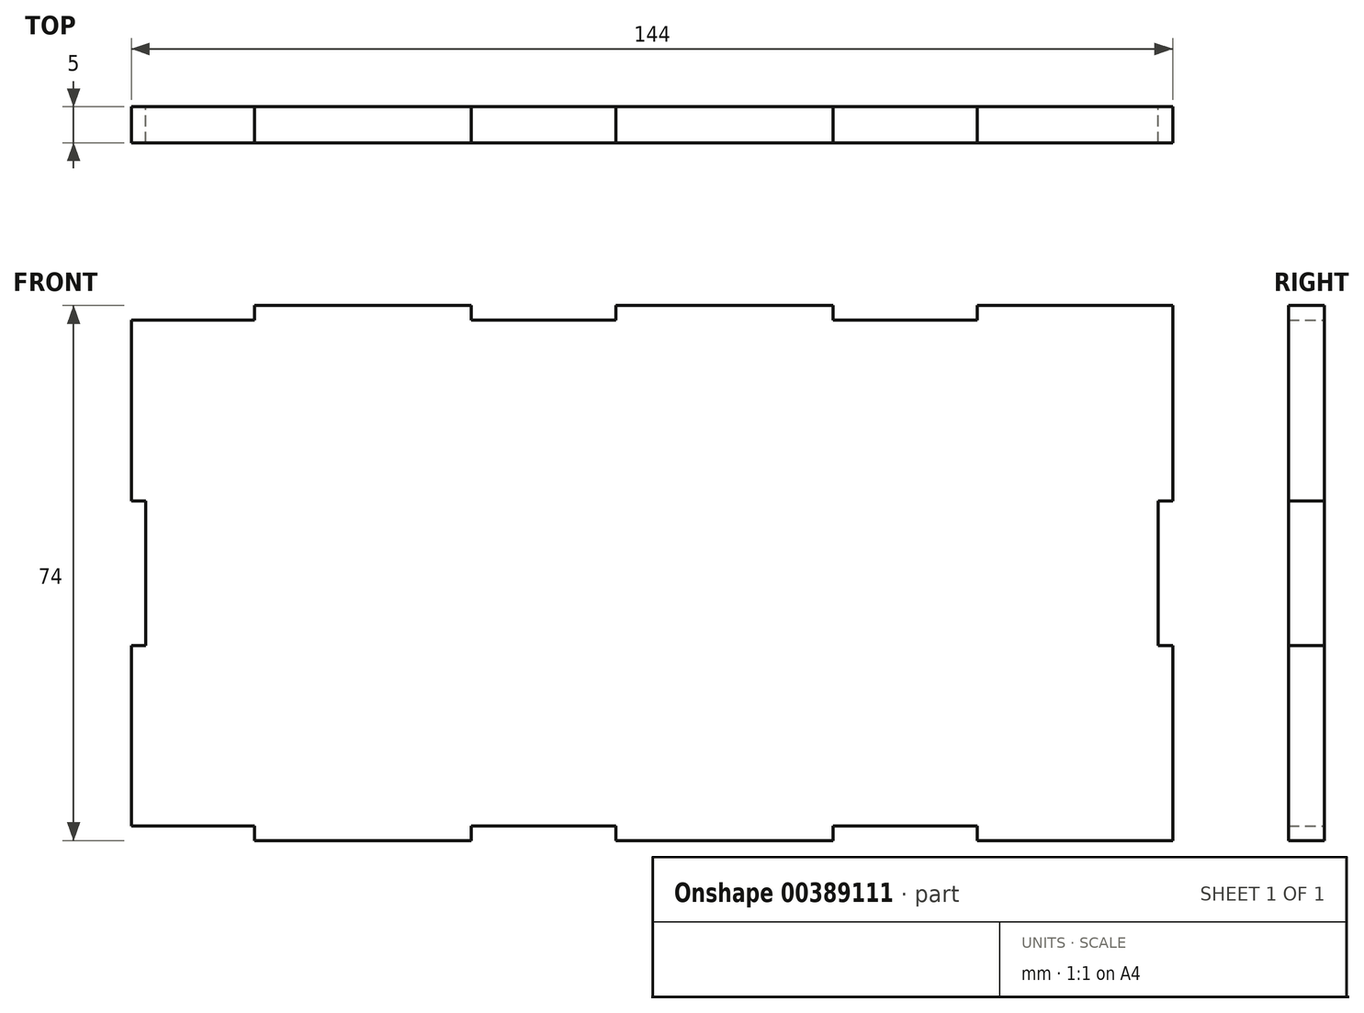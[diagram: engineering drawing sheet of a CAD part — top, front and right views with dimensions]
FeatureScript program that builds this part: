
annotation { "Feature Type Name" : "Feature", "Feature Type Description" : "" }
export const myFeature = defineFeature(function(context is Context, id is Id, definition is map)
    precondition{}
    {
        {
            var Q0;
            Q0=qCreatedBy(makeId("Front.planeOp"),FACE);
            var sketch = newSketch(context, id + "F0", { "sketchPlane" : qUnion([Q0])});
            skLineSegment(sketch, "E0", {"start": v(0, 0) * mm, "end": v(17, 0) * mm});
            skLineSegment(sketch, "E1", {"start": v(17, -2) * mm, "end": v(47, -2) * mm});
            skLineSegment(sketch, "E2", {"start": v(47, -2) * mm, "end": v(47, 0) * mm});
            skLineSegment(sketch, "E3", {"start": v(47, 0) * mm, "end": v(67, 0) * mm});
            skLineSegment(sketch, "E4", {"start": v(67, 0) * mm, "end": v(67, -2) * mm});
            skLineSegment(sketch, "E5", {"start": v(67, -2) * mm, "end": v(97, -2) * mm});
            skLineSegment(sketch, "E6", {"start": v(97, -2) * mm, "end": v(97, 0) * mm});
            skLineSegment(sketch, "E7", {"start": v(97, 0) * mm, "end": v(117, 0) * mm});
            skLineSegment(sketch, "E8", {"start": v(117, 0) * mm, "end": v(117, -2) * mm});
            skLineSegment(sketch, "E9", {"start": v(117, -2) * mm, "end": v(144, -2) * mm});
            skLineSegment(sketch, "E10", {"start": v(144, -2) * mm, "end": v(144, 25) * mm});
            skLineSegment(sketch, "E11", {"start": v(144, 25) * mm, "end": v(142, 25) * mm});
            skLineSegment(sketch, "E12", {"start": v(142, 25) * mm, "end": v(142, 45) * mm});
            skLineSegment(sketch, "E13", {"start": v(142, 45) * mm, "end": v(144, 45) * mm});
            skLineSegment(sketch, "E14", {"start": v(144, 45) * mm, "end": v(144, 72) * mm});
            skLineSegment(sketch, "E15", {"start": v(144, 72) * mm, "end": v(117, 72) * mm});
            skLineSegment(sketch, "E16", {"start": v(117, 72) * mm, "end": v(117, 70) * mm});
            skLineSegment(sketch, "E17", {"start": v(117, 70) * mm, "end": v(97, 70) * mm});
            skLineSegment(sketch, "E18", {"start": v(97, 70) * mm, "end": v(97, 72) * mm});
            skLineSegment(sketch, "E19", {"start": v(97, 72) * mm, "end": v(67, 72) * mm});
            skLineSegment(sketch, "E20", {"start": v(67, 72) * mm, "end": v(67, 70) * mm});
            skLineSegment(sketch, "E21", {"start": v(67, 70) * mm, "end": v(47, 70) * mm});
            skLineSegment(sketch, "E22", {"start": v(47, 70) * mm, "end": v(47, 72) * mm});
            skLineSegment(sketch, "E23", {"start": v(47, 72) * mm, "end": v(17, 72) * mm});
            skLineSegment(sketch, "E24", {"start": v(17, 72) * mm, "end": v(17, 70) * mm});
            skLineSegment(sketch, "E25", {"start": v(17, 70) * mm, "end": v(0, 70) * mm});
            skLineSegment(sketch, "E26", {"start": v(0, 70) * mm, "end": v(0, 45) * mm});
            skLineSegment(sketch, "E27", {"start": v(0, 45) * mm, "end": v(2, 45) * mm});
            skLineSegment(sketch, "E28", {"start": v(2, 45) * mm, "end": v(2, 25) * mm});
            skLineSegment(sketch, "E29", {"start": v(2, 25) * mm, "end": v(0, 25) * mm});
            skLineSegment(sketch, "E30", {"start": v(0, 25) * mm, "end": v(0, 0) * mm});
            skLineSegment(sketch, "E31", {"start": v(17, 0) * mm, "end": v(17, -2) * mm});
            skSolve(sketch);
        }
        {
            var Q0;
            Q0=makeQuery(id+"F0.imprint","IMPRINT",FACE,{"disambiguationData":[TD([[makeQuery(id+"F0.imprint","IMPRINT",EDGE,{"derivedFrom":sQuery(id+"F0.wireOp",EDGE,"E0")}),1.0]])]});
            extrude(context, id + "F1", {"entities" : qUnion([Q0]), "depth" : 5 * mm});
        }
    });
